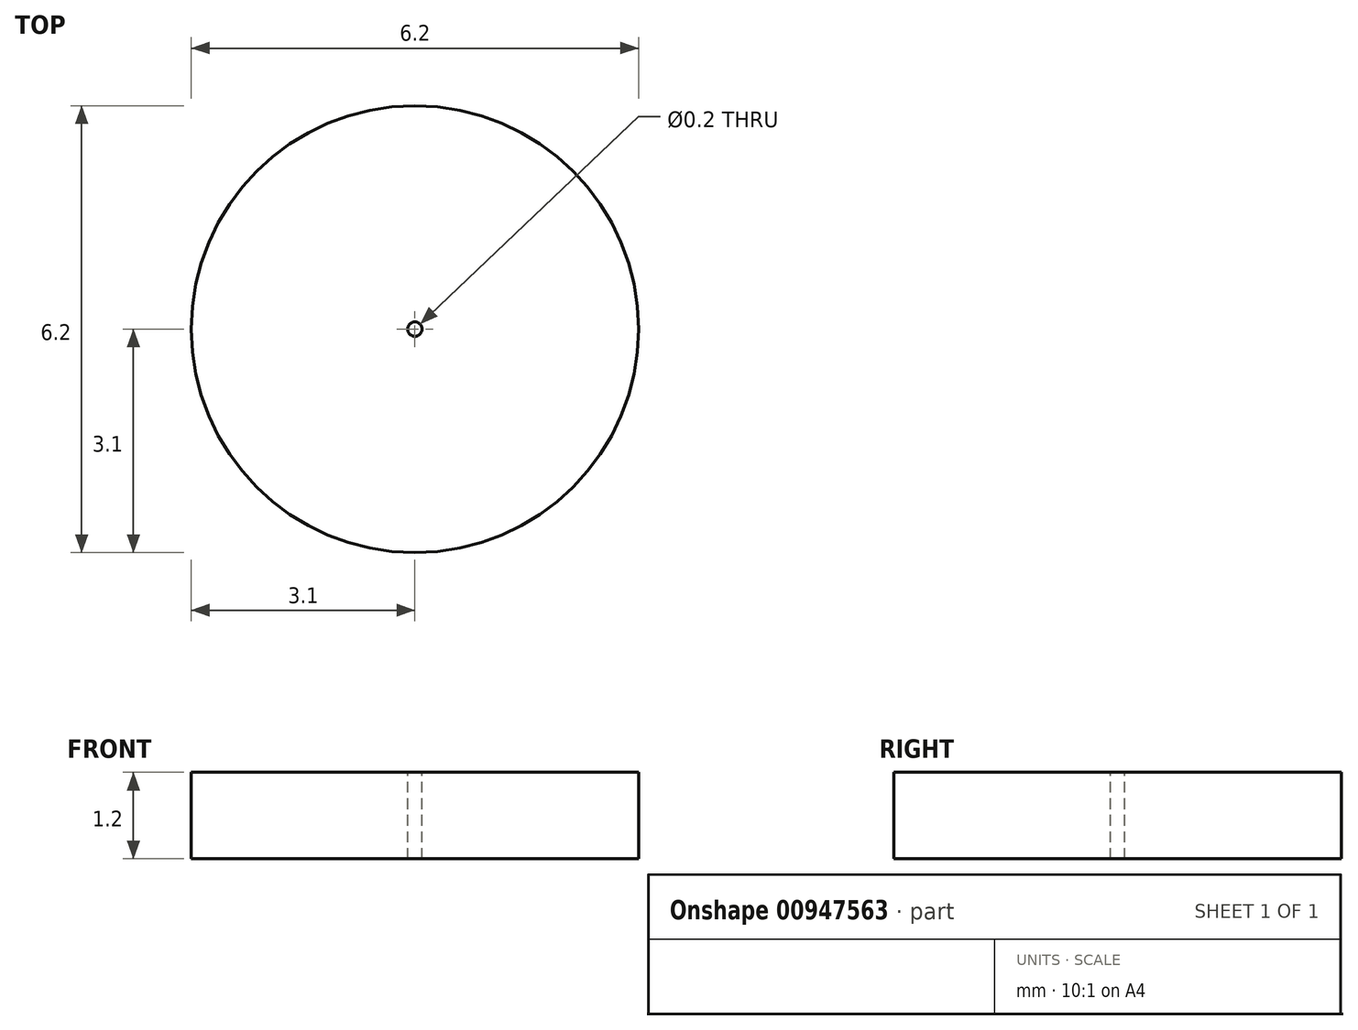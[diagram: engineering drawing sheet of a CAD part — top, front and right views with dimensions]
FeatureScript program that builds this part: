
annotation { "Feature Type Name" : "Feature", "Feature Type Description" : "" }
export const myFeature = defineFeature(function(context is Context, id is Id, definition is map)
    precondition{}
    {
        {
            var Q0;
            Q0=qCreatedBy(makeId("Top.planeOp"),FACE);
            var sketch = newSketch(context, id + "F0", { "sketchPlane" : qUnion([Q0])});
            skCircle(sketch, "E0", {"center": v(0, 0) * mm, "radius": 3.1 * mm});
            skSolve(sketch);
        }
        {
            var Q0;
            Q0=makeQuery(id+"F0.imprint","IMPRINT",FACE,{"disambiguationData":[TD([[makeQuery(id+"F0.imprint","IMPRINT",EDGE,{"derivedFrom":sQuery(id+"F0.wireOp",EDGE,"E0")}),1.0]])]});
            extrude(context, id + "F1", {"entities" : qUnion([Q0]), "depth" : 1.2 * mm, "offsetDistance" : 25.4 * mm});
        }
        {
            var Q0;
            Q0=makeQuery(id+"F1.opExtrude","CAP_FACE",FACE,{"disambiguationData":[OSD([sQuery(id+"F0.wireOp",EDGE,"E0")])],"isStart":false});
            var sketch = newSketch(context, id + "F2", { "sketchPlane" : qUnion([Q0])});
            skCircle(sketch, "E1", {"center": v(0, 0) * mm, "radius": 0.1 * mm});
            skSolve(sketch);
        }
        {
            var Q0;
            Q0 = qSketchRegion(id + "F2", true);
            var Q1;
            Q1=makeQuery(id+"F1.opExtrude","CAP_FACE",FACE,{"disambiguationData":[OSD([sQuery(id+"F0.wireOp",EDGE,"E0")])],"isStart":true});
            extrude(context, id + "F3", {"entities" : qUnion([Q0]), "operationType" : NewBodyOperationType.REMOVE, "endBound" : BoundingType.UP_TO_SURFACE, "oppositeDirection" : true, "depth" : 25.4 * mm, "endBoundEntityFace" : qUnion([Q1]), "offsetDistance" : 25.4 * mm});
        }
    });
